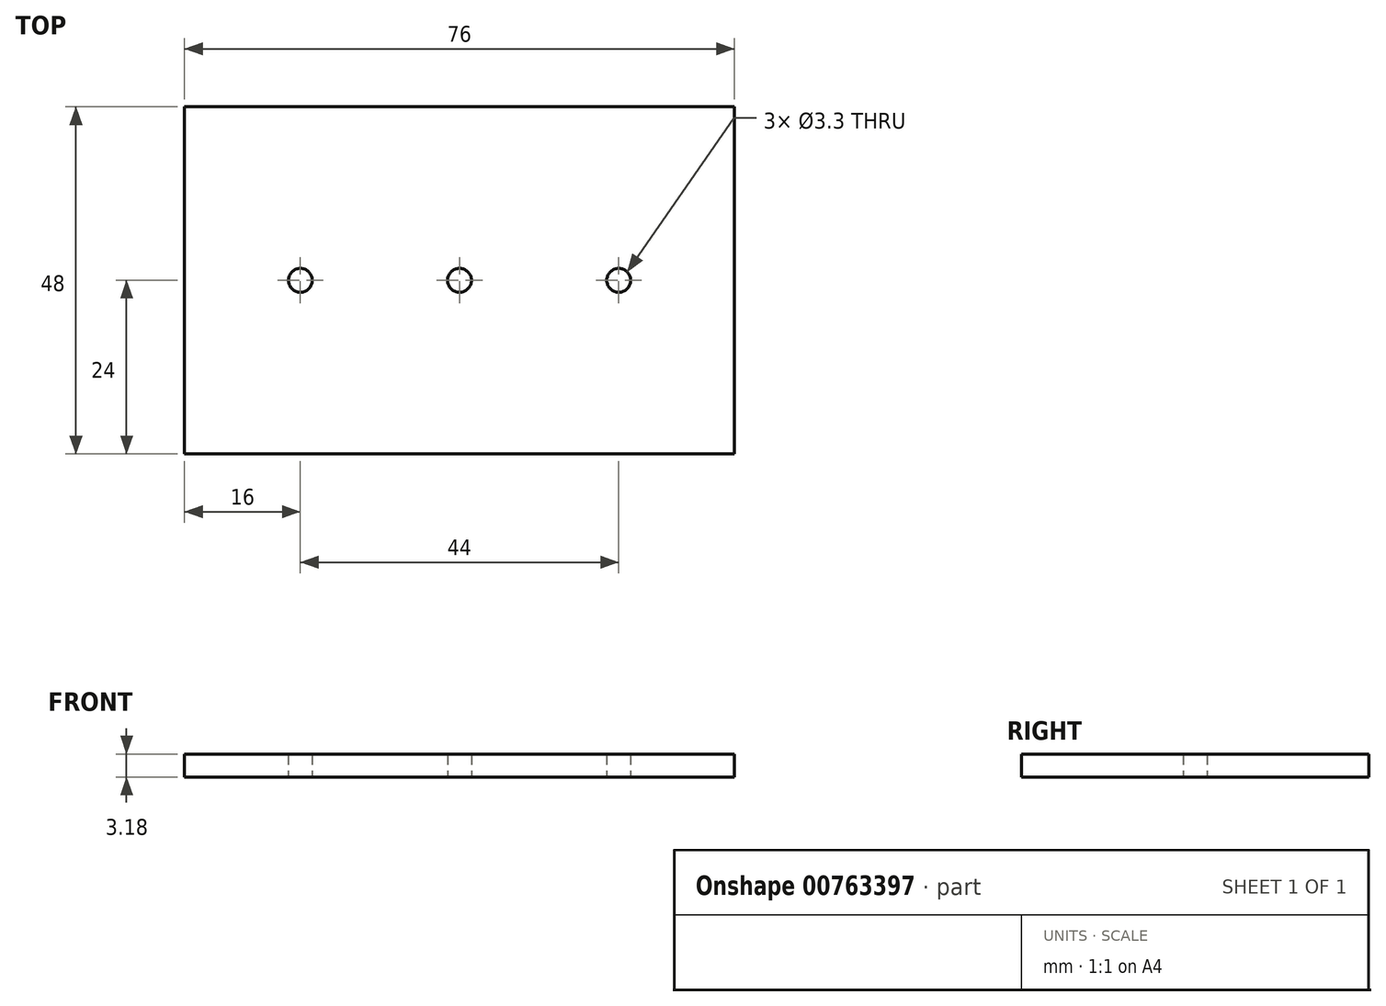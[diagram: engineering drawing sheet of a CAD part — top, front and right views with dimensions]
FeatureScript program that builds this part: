
annotation { "Feature Type Name" : "Feature", "Feature Type Description" : "" }
export const myFeature = defineFeature(function(context is Context, id is Id, definition is map)
    precondition{}
    {
        {
            var Q0;
            Q0=qCreatedBy(makeId("Top.planeOp"),FACE);
            var sketch = newSketch(context, id + "F0", { "sketchPlane" : qUnion([Q0])});
            skLineSegment(sketch, "E0.bottom", {"start": v(0, 0) * mm, "end": v(76, 0) * mm});
            skLineSegment(sketch, "E0.top", {"start": v(0, 48) * mm, "end": v(76, 48) * mm});
            skLineSegment(sketch, "E0.left", {"start": v(0, 0) * mm, "end": v(0, 48) * mm});
            skLineSegment(sketch, "E0.right", {"start": v(76, 0) * mm, "end": v(76, 48) * mm});
            skPoint(sketch, "E1", {"position": v(16, 24) * mm});
            skPoint(sketch, "E2", {"position": v(60, 24) * mm});
            skCircle(sketch, "E3", {"center": v(16, 24) * mm, "radius": 1.65 * mm});
            skCircle(sketch, "E4", {"center": v(38, 24) * mm, "radius": 1.65 * mm});
            skCircle(sketch, "E5", {"center": v(60, 24) * mm, "radius": 1.65 * mm});
            skSolve(sketch);
        }
        {
            var Q0;
            Q0=makeQuery(id+"F0.imprint","IMPRINT",FACE,{"disambiguationData":[TD([[makeQuery(id+"F0.imprint","IMPRINT",EDGE,{"derivedFrom":sQuery(id+"F0.wireOp",EDGE,"E0.bottom")}),1.0]])]});
            extrude(context, id + "F1", {"entities" : qUnion([Q0]), "depth" : 3.17 * mm, "offsetDistance" : 25.4 * mm});
        }
    });
